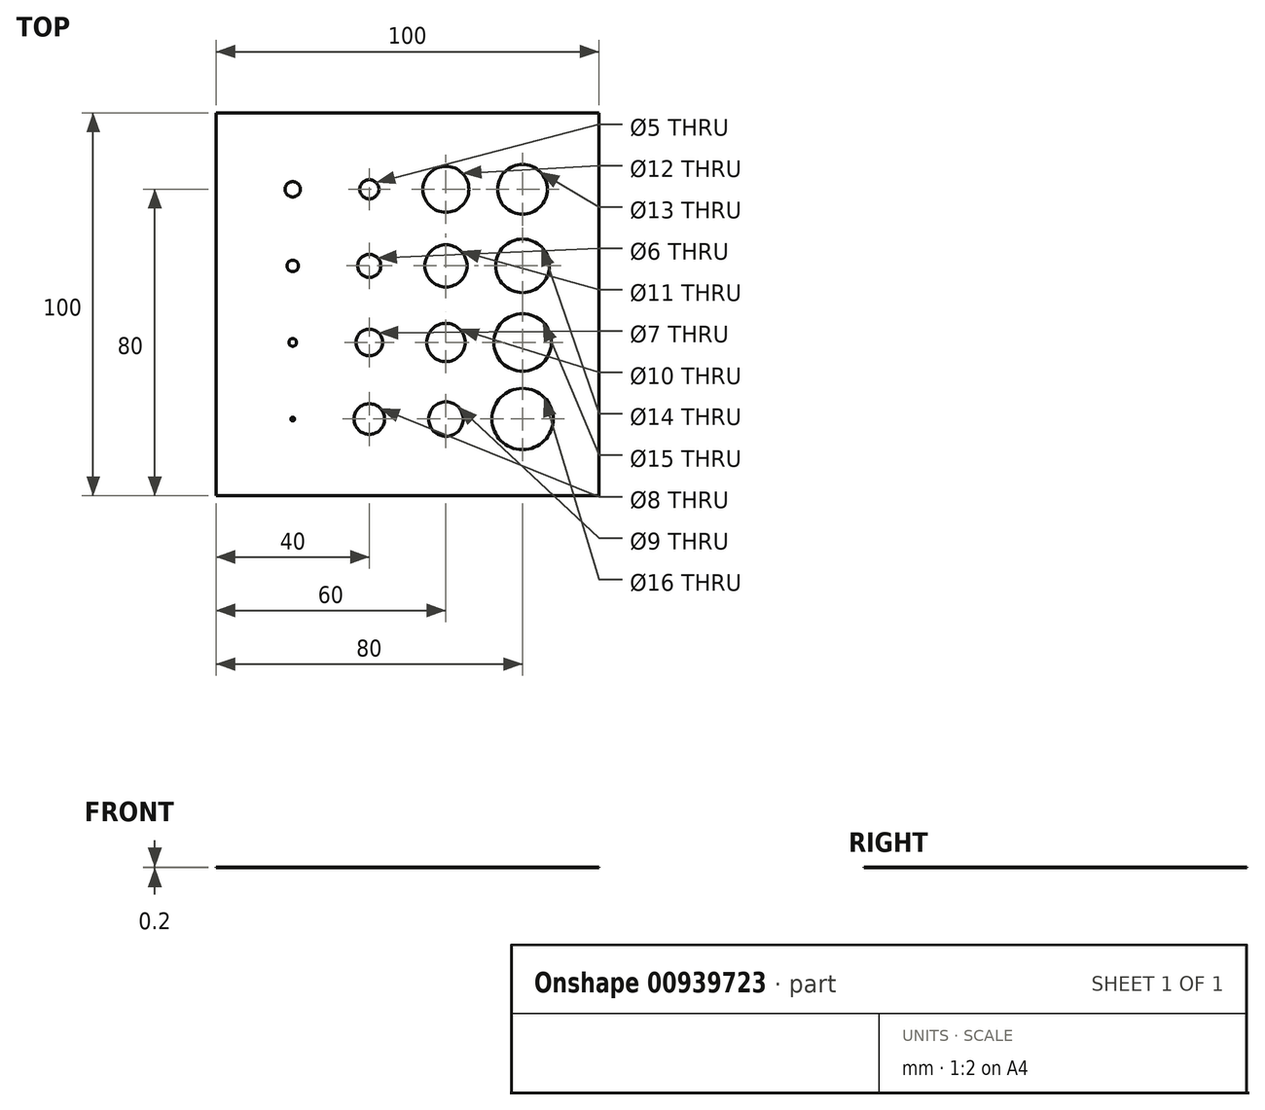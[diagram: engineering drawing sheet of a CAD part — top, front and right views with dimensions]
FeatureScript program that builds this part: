
annotation { "Feature Type Name" : "Feature", "Feature Type Description" : "" }
export const myFeature = defineFeature(function(context is Context, id is Id, definition is map)
    precondition{}
    {
        {
            var Q0;
            Q0=qCreatedBy(makeId("Top.planeOp"),FACE);
            var sketch = newSketch(context, id + "F0", { "sketchPlane" : qUnion([Q0])});
            skLineSegment(sketch, "E0.bottom", {"start": v(0, 0) * mm, "end": v(100, 0) * mm});
            skLineSegment(sketch, "E0.top", {"start": v(0, 100) * mm, "end": v(100, 100) * mm});
            skLineSegment(sketch, "E0.left", {"start": v(0, 0) * mm, "end": v(0, 100) * mm});
            skLineSegment(sketch, "E0.right", {"start": v(100, 0) * mm, "end": v(100, 100) * mm});
            skLineSegment(sketch, "E1", {"start": v(80, 0) * mm, "end": v(80, 20) * mm, "construction": true});
            skLineSegment(sketch, "E2", {"start": v(80, 20) * mm, "end": v(100, 20) * mm, "construction": true});
            skLineSegment(sketch, "E3", {"start": v(80, 20) * mm, "end": v(60, 20) * mm, "construction": true});
            skLineSegment(sketch, "E4", {"start": v(60, 20) * mm, "end": v(40, 20) * mm, "construction": true});
            skLineSegment(sketch, "E5", {"start": v(40, 20) * mm, "end": v(20, 20) * mm, "construction": true});
            skLineSegment(sketch, "E6", {"start": v(80, 20) * mm, "end": v(80, 40) * mm, "construction": true});
            skLineSegment(sketch, "E7", {"start": v(80, 40) * mm, "end": v(80, 60) * mm, "construction": true});
            skLineSegment(sketch, "E8", {"start": v(80, 60) * mm, "end": v(80, 80) * mm, "construction": true});
            skLineSegment(sketch, "E9", {"start": v(80, 40) * mm, "end": v(60, 40) * mm, "construction": true});
            skLineSegment(sketch, "E10", {"start": v(60, 40) * mm, "end": v(40, 40) * mm, "construction": true});
            skLineSegment(sketch, "E11", {"start": v(40, 40) * mm, "end": v(20, 40) * mm, "construction": true});
            skLineSegment(sketch, "E12", {"start": v(80, 60) * mm, "end": v(60, 60) * mm, "construction": true});
            skLineSegment(sketch, "E13", {"start": v(60, 60) * mm, "end": v(40, 60) * mm, "construction": true});
            skLineSegment(sketch, "E14", {"start": v(40, 60) * mm, "end": v(20, 60) * mm, "construction": true});
            skLineSegment(sketch, "E15", {"start": v(80, 80) * mm, "end": v(60, 80) * mm, "construction": true});
            skLineSegment(sketch, "E16", {"start": v(60, 80) * mm, "end": v(40, 80) * mm, "construction": true});
            skLineSegment(sketch, "E17", {"start": v(40, 80) * mm, "end": v(20, 80) * mm, "construction": true});
            skCircle(sketch, "E18", {"center": v(80, 20) * mm, "radius": 8 * mm});
            skCircle(sketch, "E19", {"center": v(60, 20) * mm, "radius": 4.5 * mm});
            skCircle(sketch, "E20", {"center": v(40, 20) * mm, "radius": 4 * mm});
            skCircle(sketch, "E21", {"center": v(20, 20) * mm, "radius": 0.5 * mm});
            skCircle(sketch, "E22", {"center": v(80, 40) * mm, "radius": 7.5 * mm});
            skCircle(sketch, "E23", {"center": v(80, 60) * mm, "radius": 7 * mm});
            skCircle(sketch, "E24", {"center": v(60, 40) * mm, "radius": 5 * mm});
            skCircle(sketch, "E25", {"center": v(40, 40) * mm, "radius": 3.5 * mm});
            skCircle(sketch, "E26", {"center": v(20, 40) * mm, "radius": 1 * mm});
            skCircle(sketch, "E27", {"center": v(60, 60) * mm, "radius": 5.5 * mm});
            skCircle(sketch, "E28", {"center": v(40, 60) * mm, "radius": 3 * mm});
            skCircle(sketch, "E29", {"center": v(20, 60) * mm, "radius": 1.5 * mm});
            skCircle(sketch, "E30", {"center": v(80, 80) * mm, "radius": 6.5 * mm});
            skCircle(sketch, "E31", {"center": v(60, 80) * mm, "radius": 6 * mm});
            skCircle(sketch, "E32", {"center": v(40, 80) * mm, "radius": 2.5 * mm});
            skCircle(sketch, "E33", {"center": v(20, 80) * mm, "radius": 2 * mm});
            skSolve(sketch);
        }
        {
            var Q0;
            Q0=makeQuery(id+"F0.imprint","IMPRINT",FACE,{"disambiguationData":[TD([[makeQuery(id+"F0.imprint","IMPRINT",EDGE,{"derivedFrom":sQuery(id+"F0.wireOp",EDGE,"E0.bottom")}),1.0]])]});
            extrude(context, id + "F1", {"entities" : qUnion([Q0]), "depth" : 0.2 * mm, "offsetDistance" : 25 * mm});
        }
    });
